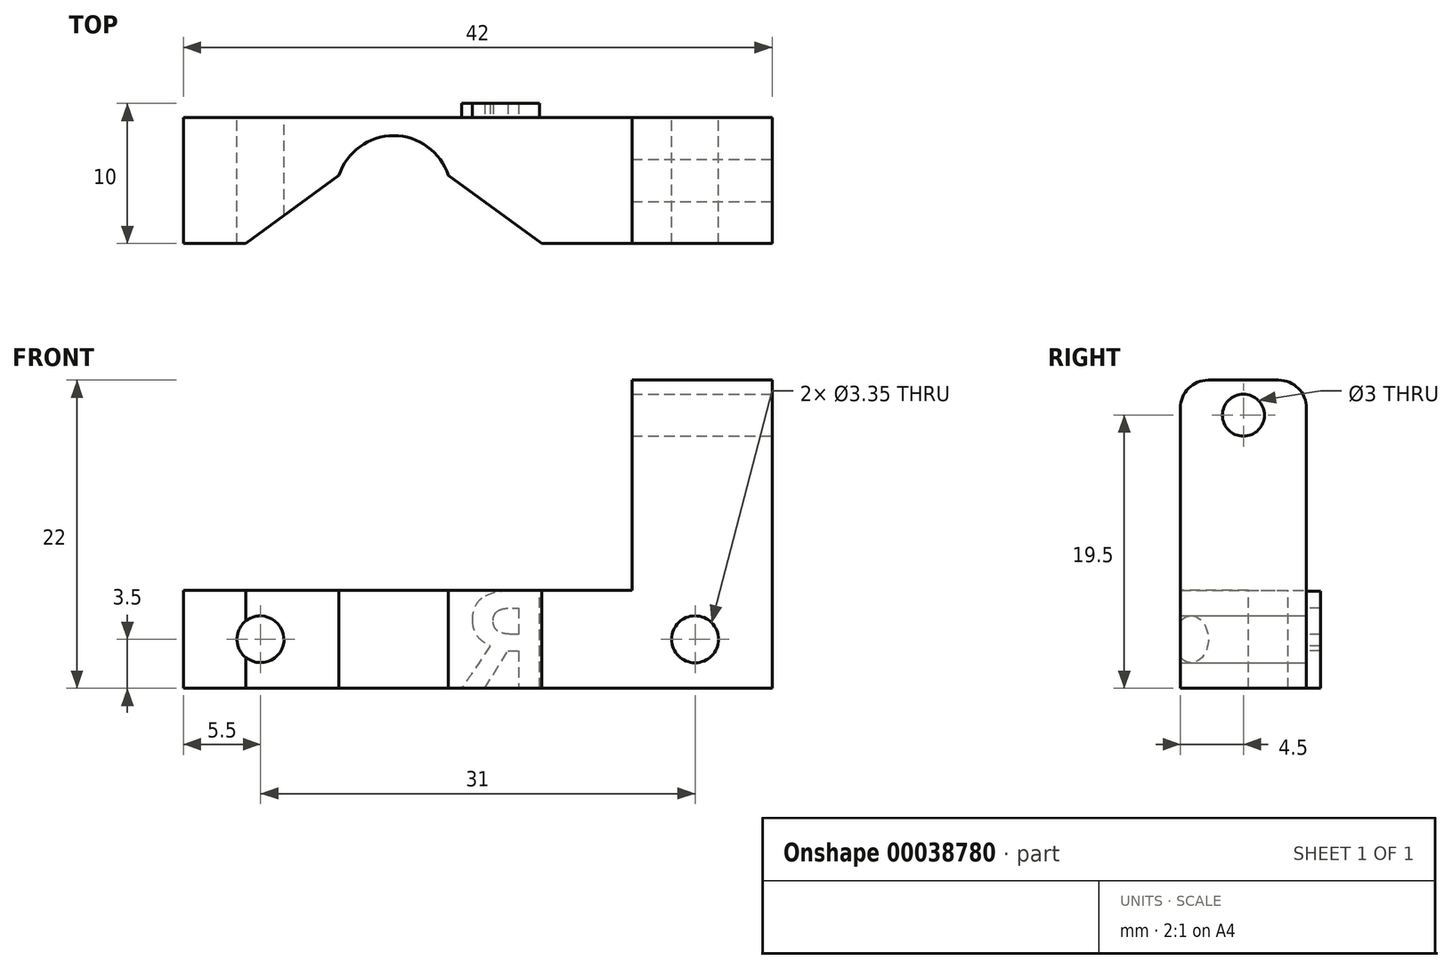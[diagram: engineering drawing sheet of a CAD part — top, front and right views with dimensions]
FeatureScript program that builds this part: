
annotation { "Feature Type Name" : "Feature", "Feature Type Description" : "" }
export const myFeature = defineFeature(function(context is Context, id is Id, definition is map)
    precondition{}
    {
        {
            assignVariable(context, id + "F0", {"name" : "rods", "anyValue" : 8});
        }
        {
            var Q0;
            Q0=qCreatedBy(makeId("Top.planeOp"),FACE);
            var sketch = newSketch(context, id + "F1", { "sketchPlane" : qUnion([Q0])});
            skLineSegment(sketch, "E0.bottom", {"start": v(0, 0) * mm, "end": v(42, 0) * mm});
            skLineSegment(sketch, "E0.top", {"start": v(0, 9) * mm, "end": v(42, 9) * mm});
            skLineSegment(sketch, "E0.left", {"start": v(0, 0) * mm, "end": v(0, 9) * mm});
            skLineSegment(sketch, "E0.right", {"start": v(42, 0) * mm, "end": v(42, 9) * mm});
            skSolve(sketch);
        }
        {
            var Q0;
            Q0=qSketchRegion(id+"F1",true);
            extrude(context, id + "F2", {"entities" : qUnion([Q0]), "depth" : 7 * mm});
        }
        {
            var Q0;
            Q0=makeQuery(id+"F2.opExtrude","CAP_FACE",FACE,{"disambiguationData":[OSD([sQuery(id+"F1.wireOp",EDGE,"E0.bottom"),sQuery(id+"F1.wireOp",EDGE,"E0.top"),sQuery(id+"F1.wireOp",EDGE,"E0.left"),sQuery(id+"F1.wireOp",EDGE,"E0.right")])],"isStart":false});
            var sketch = newSketch(context, id + "F3", { "sketchPlane" : qUnion([Q0])});
            skCircle(sketch, "E1", {"center": v(15, 3.6) * mm, "radius": 4.1 * mm});
            skSolve(sketch);
        }
        {
            var Q0;
            Q0=qSketchRegion(id+"F3",true);
            extrude(context, id + "F4", {"entities" : qUnion([Q0]), "operationType" : NewBodyOperationType.REMOVE, "oppositeDirection" : true, "depth" : 25 * mm});
        }
        {
            var Q0;
            Q0=makeQuery(id+"F4.boolean.opBoolean","INTERSECT",EDGE,{"disambiguationData":[OD(0.0)],"derivedFrom":[makeQuery(id+"F2.opExtrude","SWEPT_FACE",FACE,{"disambiguationData":[OSD([sQuery(id+"F1.wireOp",EDGE,"E0.bottom")])]}),makeQuery(id+"F4.opExtrude","SWEPT_FACE",FACE,{"disambiguationData":[OSD([sQuery(id+"F3.wireOp",EDGE,"E1")])]})]});
            var Q1;
            Q1=makeQuery(id+"F4.boolean.opBoolean","INTERSECT",EDGE,{"disambiguationData":[OD(1.0)],"derivedFrom":[makeQuery(id+"F2.opExtrude","SWEPT_FACE",FACE,{"disambiguationData":[OSD([sQuery(id+"F1.wireOp",EDGE,"E0.bottom")])]}),makeQuery(id+"F4.opExtrude","SWEPT_FACE",FACE,{"disambiguationData":[OSD([sQuery(id+"F3.wireOp",EDGE,"E1")])]})]});
            chamfer(context, id + "F5", {"entities" : qUnion([Q0, Q1]), "width" : (getVariable(context, 'rods') - 1) * mm, "tangentPropagation" : true});
        }
        {
            var Q0;
            Q0=makeQuery(id+"F2.opExtrude","SWEPT_FACE",FACE,{"disambiguationData":[OSD([sQuery(id+"F1.wireOp",EDGE,"E0.top")])]});
            var sketch = newSketch(context, id + "F6", { "sketchPlane" : qUnion([Q0])});
            skCircle(sketch, "E2", {"center": v(-5.5, 3.5) * mm, "radius": 1.68 * mm});
            skCircle(sketch, "E3", {"center": v(-36.5, 3.5) * mm, "radius": 1.68 * mm});
            skLineSegment(sketch, "E4", {"start": v(-5.5, 0) * mm, "end": v(-5.5, 7) * mm});
            skLineSegment(sketch, "E5", {"start": v(-5.5, 3.5) * mm, "end": v(0, 3.5) * mm});
            skLineSegment(sketch, "E6", {"start": v(-36.5, 3.5) * mm, "end": v(-42, 3.5) * mm});
            skSolve(sketch);
        }
        {
            var Q0;
            Q0=qSketchRegion(id+"F6",true);
            extrude(context, id + "F7", {"entities" : qUnion([Q0]), "operationType" : NewBodyOperationType.REMOVE, "oppositeDirection" : true, "depth" : 25 * mm});
        }
        {
            var Q0;
            Q0=makeQuery(id+"F2.opExtrude","SWEPT_FACE",FACE,{"disambiguationData":[OSD([sQuery(id+"F1.wireOp",EDGE,"E0.top")])]});
            var sketch = newSketch(context, id + "F8", { "sketchPlane" : qUnion([Q0])});
            skText(sketch, "E7", { "text": "R", "fontName": "OpenSans-Bold.ttf"});
            const initialGuessF8  = {"E7": [-0.02627, 0, 1, 0, 0.007]};
            skSetInitialGuess(sketch, initialGuessF8);
            skSolve(sketch);
        }
        {
            var Q0;
            Q0=qSketchRegion(id+"F8",true);
            extrude(context, id + "F9", {"entities" : qUnion([Q0]), "operationType" : NewBodyOperationType.ADD, "depth" : 1 * mm});
        }
        {
            var Q0;
            Q0=makeQuery(id+"F2.opExtrude","CAP_FACE",FACE,{"disambiguationData":[OSD([sQuery(id+"F1.wireOp",EDGE,"E0.bottom"),sQuery(id+"F1.wireOp",EDGE,"E0.top"),sQuery(id+"F1.wireOp",EDGE,"E0.left"),sQuery(id+"F1.wireOp",EDGE,"E0.right")])],"isStart":false});
            var sketch = newSketch(context, id + "F10", { "sketchPlane" : qUnion([Q0])});
            skLineSegment(sketch, "E8.bottom", {"start": v(42, 0) * mm, "end": v(32, 0) * mm});
            skLineSegment(sketch, "E8.top", {"start": v(42, 9) * mm, "end": v(32, 9) * mm});
            skLineSegment(sketch, "E8.left", {"start": v(42, 0) * mm, "end": v(42, 9) * mm});
            skLineSegment(sketch, "E8.right", {"start": v(32, 0) * mm, "end": v(32, 9) * mm});
            skSolve(sketch);
        }
        {
            var Q0;
            Q0=qSketchRegion(id+"F10",true);
            extrude(context, id + "F11", {"entities" : qUnion([Q0]), "operationType" : NewBodyOperationType.ADD, "depth" : 15 * mm});
        }
        {
            var Q0;
            Q0=makeQuery(id+"FJdLS7F1L1csLPb_1.boolean.opBoolean","MERGE",FACE,{"derivedFrom":[makeQuery(id+"F11.boolean.opBoolean","MERGE",FACE,{"derivedFrom":[makeQuery(id+"F2.opExtrude","SWEPT_FACE",FACE,{"disambiguationData":[OSD([sQuery(id+"F1.wireOp",EDGE,"E0.right")])]}),makeQuery(id+"F11.opExtrude","SWEPT_FACE",FACE,{"disambiguationData":[OSD([sQuery(id+"F10.wireOp",EDGE,"E8.left")])]})]}),makeQuery(id+"FJdLS7F1L1csLPb_1.opExtrude","SWEPT_FACE",FACE,{"disambiguationData":[OSD([sQuery(id+"F4Ds6MLMi3WL0gL_1.wireOp",EDGE,"f6963c6d-1d98-4eef-b5cd-deae189cd3ae.left")])]})]});
            var sketch = newSketch(context, id + "F12", { "sketchPlane" : qUnion([Q0])});
            skCircle(sketch, "E9", {"center": v(4.5, 19.5) * mm, "radius": 1.5 * mm});
            skPoint(sketch, "E10", {"position": v(0, 19.5) * mm});
            skPoint(sketch, "E11", {"position": v(4.5, 0) * mm});
            skSolve(sketch);
        }
        {
            var Q0;
            Q0=qSketchRegion(id+"F12",true);
            extrude(context, id + "F13", {"entities" : qUnion([Q0]), "operationType" : NewBodyOperationType.REMOVE, "oppositeDirection" : true, "depth" : 25 * mm});
        }
        {
            var Q0;
            Q0=makeQuery(id+"F11.opExtrude","CAP_EDGE",EDGE,{"disambiguationData":[OSD([sQuery(id+"F10.wireOp",EDGE,"E8.bottom")])],"isStart":false});
            var Q1;
            Q1=makeQuery(id+"F11.opExtrude","CAP_EDGE",EDGE,{"disambiguationData":[OSD([sQuery(id+"F10.wireOp",EDGE,"E8.top")])],"isStart":false});
            fillet(context, id + "F14", {"entities" : qUnion([Q0, Q1]), "radius" : 2 * mm, "tangentPropagation" : true, "allowEdgeOverflow" : false});
        }
    });
